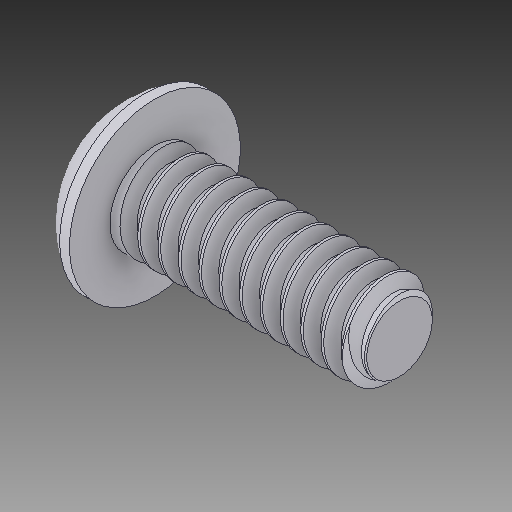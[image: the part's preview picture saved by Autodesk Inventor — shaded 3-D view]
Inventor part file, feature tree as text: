
AUTODESK INVENTOR PART (.ipt)
format: ipt  version: 2018 (Build 220112000, 112)  size: 516,096 bytes
history: native  units: in
note: dims shown in document units (in); Inventor stores cm internally (conversion verified against a paired STEP export)
features: thread x1
ambient origin geometry x8: Origin, YZ Plane, XZ Plane, XY Plane, X Axis, Y Axis, Z Axis, Center Point
bodies: Solid1 (feature_tree)
feature tree (1):
  thread  "Thread1"  [1 undecoded]
note: 1 required parameter value undecoded (feature->parameter linkage not recoverable at this tier; creation-order binding heuristic only, values carry confidence <= 0.55)
